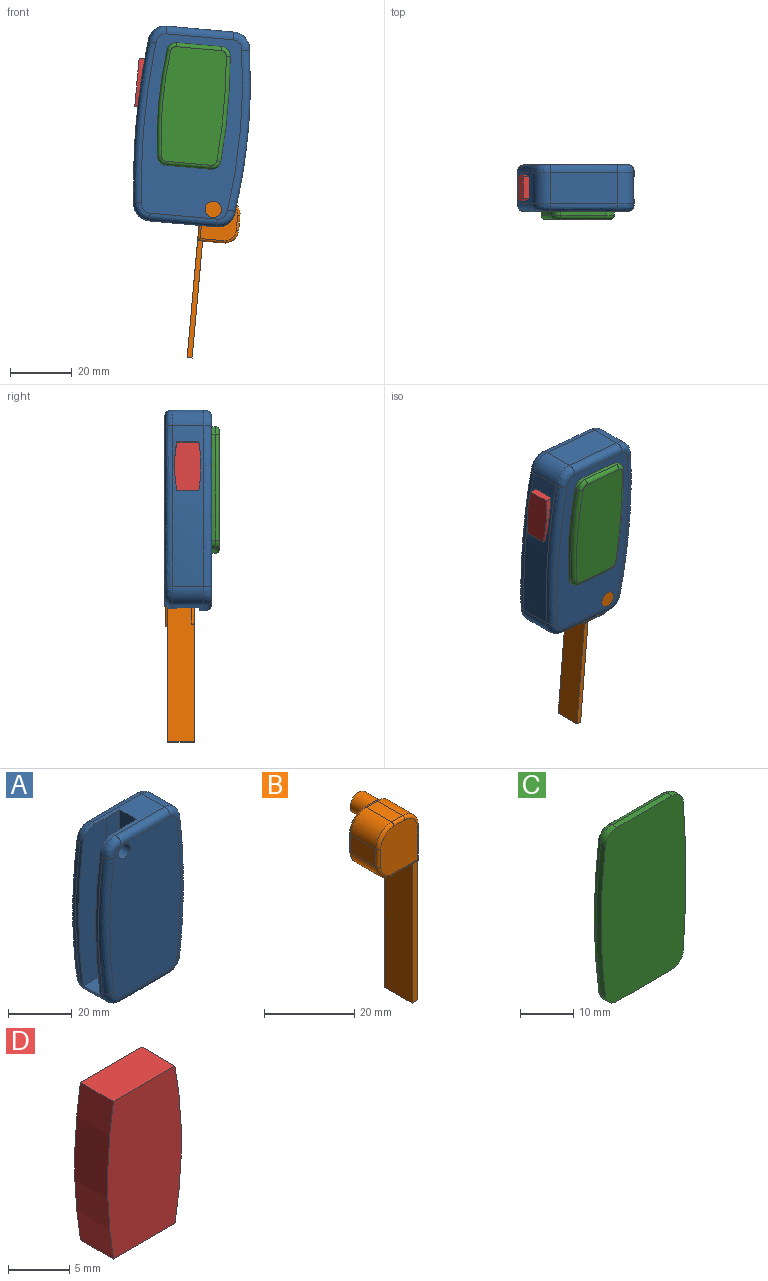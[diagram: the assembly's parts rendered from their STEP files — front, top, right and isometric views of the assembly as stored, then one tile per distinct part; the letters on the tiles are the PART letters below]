
ASSEMBLY  parts=4 mates=3
PART A: 44 faces, bbox 36.5x15.3x63.5 mm
  f0: plane 59.69x7.5mm, normal (-1,0,0), area 368.2mm2, adj f1,f29,f30,f31,f34,f35
  f1: plane 21.84x10.16mm, normal (0,0,1), area 141.2mm2, adj f0,f2,f7,f8,f16,f24,f29,f30
  f2: cylinder r=5.59mm len=5.59mm, axis (0,1,0), area 11.9mm2, adj f1,f3,f26,f29
  f3: cylinder r=183.3mm len=52.32mm, axis (0,1,0), area 71mm2, adj f2,f4,f28,f29
  f4: cylinder r=5.59mm len=10.16mm, axis (0,1,0), area 75.6mm2, adj f3,f9,f10,f19,f27,f29,f30,f31
  f5: cylinder r=5.59mm len=10.16mm, axis (0,1,0), area 89.2mm2, adj f6,f10,f15,f23
  f6: cylinder r=223.52mm len=52.32mm, axis (0,1,0), area 464.3mm2, adj f5,f7,f13,f21,f38,f39,f40,f41
  f7: cylinder r=5.59mm len=10.16mm, axis (0,1,0), area 89.2mm2, adj f1,f6,f14,f22
  f8: cylinder r=5.59mm len=5.59mm, axis (0,1,0), area 11.5mm2, adj f1,f9,f18,f30
  f9: cylinder r=183.3mm len=52.32mm, axis (0,1,0), area 68.7mm2, adj f4,f8,f20,f30
  f10: plane 21.84x10.16mm, normal (0,0,-1), area 221.9mm2, adj f4,f5,f17,f25
  f11: plane 58.43x31.36mm, normal (0,-1,0), area 1720.3mm2, adj f13,f14,f15,f16,f17,f18,f19,f20
  f12: plane 58.43x31.36mm, normal (0,1,0), area 1742.6mm2, adj f21,f22,f23,f24,f25,f26,f27,f28
  f13: bspline ~52.67x4.08mm, area 216.5mm2, adj f6,f11,f14,f15
  f14: bspline ~5.82x5.59mm, area 31mm2, adj f7,f11,f13,f16
  f15: bspline ~6.17x5.62mm, area 31mm2, adj f5,f11,f13,f17
  f16: bspline ~21.84x2.54mm, area 90.2mm2, adj f1,f11,f14,f18
  f17: bspline ~21.84x2.54mm, area 90.2mm2, adj f10,f11,f15,f19
  f18: bspline ~6.22x5.62mm, area 31.1mm2, adj f8,f11,f16,f20
  f19: bspline ~6.22x5.62mm, area 31.1mm2, adj f4,f11,f17,f20
  f20: bspline ~56.81x4.79mm, area 216.7mm2, adj f9,f11,f18,f19
  f21: bspline ~52.67x4.08mm, area 216.5mm2, adj f6,f12,f22,f23
  f22: bspline ~6.17x5.62mm, area 31mm2, adj f7,f12,f21,f24
  f23: bspline ~5.82x5.59mm, area 31mm2, adj f5,f12,f21,f25
  f24: bspline ~21.84x2.54mm, area 90.2mm2, adj f1,f12,f22,f26
  f25: bspline ~21.84x2.54mm, area 90.2mm2, adj f10,f12,f23,f27
  f26: bspline ~6.22x5.62mm, area 31.1mm2, adj f2,f12,f24,f28
  f27: bspline ~6.22x5.62mm, area 31.1mm2, adj f4,f12,f25,f28
  f28: bspline ~56.81x4.79mm, area 216.7mm2, adj f3,f12,f26,f27
  f29: plane 59.69x12.22mm, normal (0,-1,0), area 675.8mm2, adj f0,f1,f2,f3,f4,f31,f32
  f30: plane 59.69x12.22mm, normal (0,1,0), area 653.4mm2, adj f0,f1,f4,f8,f9,f31,f37
  f31: plane 10.05x7.5mm, normal (0,0,1), area 75.3mm2, adj f0,f4,f29,f30
  f32: plane 10.75x0.02mm, normal (1,0,0), area 0.2mm2, adj f1,f29,f33,f35
  f33: plane 10.75x6.1mm, normal (0,-1,0), area 65.6mm2, adj f1,f32,f35,f36
  f34: plane 10.75x6.1mm, normal (0,1,0), area 65.6mm2, adj f0,f1,f35,f36
  f35: plane 7.41x6.1mm, normal (0,0,1), area 45.1mm2, adj f0,f32,f33,f34,f36
  f36: plane 10.75x7.41mm, normal (-1,0,0), area 79.6mm2, adj f1,f33,f34,f35
  f37: cylinder r=2.67mm len=5.33mm, axis (0,1,0), area 64.5mm2, adj f11,f30
  f38: cylinder r=47.15mm len=15.75mm, axis (1,0,0), area 37.3mm2, adj f6,f39,f41,f42,f43
  f39: plane 7.11x1.88mm, normal (0,0,1), area 13.4mm2, adj f6,f38,f40,f43
  f40: cylinder r=42.58mm len=15.75mm, axis (1,0,0), area 37.3mm2, adj f6,f39,f41,f42,f43
  f41: plane 8.49x6.98mm, normal (-1,0,0), area 55.8mm2, adj f6,f38,f40,f42
  f42: plane 7.11x2.54mm, normal (0,0,-1), area 18.1mm2, adj f38,f40,f41,f43
  f43: plane 15.75x8.51mm, normal (1,0,0), area 126.7mm2, adj f38,f39,f40,f42
PART B: 30 faces, bbox 13.8x15x52.7 mm
  f0: plane 7.87x6.83mm, normal (0,0,-1), area 53.8mm2, adj f6,f15,f22,f23
  f1: plane 47.7x8.64mm, normal (1,0,0), area 404.8mm2, adj f2,f14,f21,f24,f25,f26,f27
  f2: cylinder r=4.61mm len=7.87mm, axis (0,1,0), area 57.1mm2, adj f1,f3,f12,f19
  f3: plane 7.87x3.45mm, normal (0,0,1), area 27.1mm2, adj f2,f4,f10,f17
  f4: cylinder r=4.92mm len=7.87mm, axis (0,1,0), area 60.9mm2, adj f3,f5,f9,f16
  f5: plane 7.87x4.79mm, normal (-1,0,0), area 37.7mm2, adj f4,f6,f11,f18
  f6: cylinder r=4.52mm len=7.87mm, axis (0,1,0), area 55.9mm2, adj f0,f5,f13,f20
  f7: plane 12.71x11.46mm, normal (0,-1,0), area 135.7mm2, adj f9,f10,f11,f12,f13,f14,f15
  f8: plane 12.71x11.46mm, normal (0,1,0), area 113.3mm2, adj f16,f17,f18,f19,f20,f21,f22,f28
  f9: torus R=4.16mm, axis (0,-1,0), area 8.7mm2, adj f4,f7,f10,f11
  f10: cylinder r=0.76mm len=3.45mm, axis (1,0,0), area 4.1mm2, adj f3,f7,f9,f12
  f11: cylinder r=0.76mm len=4.79mm, axis (0,0,1), area 5.7mm2, adj f5,f7,f9,f13
  f12: torus R=3.85mm, axis (0,-1,0), area 8.2mm2, adj f2,f7,f10,f14
  f13: torus R=3.76mm, axis (0,-1,0), area 8mm2, adj f6,f7,f11,f15
  f14: cylinder r=0.76mm len=9.62mm, axis (0,0,-1), area 11.2mm2, adj f1,f7,f12,f15
  f15: cylinder r=0.76mm len=8.47mm, axis (-1,0,0), area 9.8mm2, adj f0,f7,f13,f14,f26
  f16: torus R=4.16mm, axis (0,-1,0), area 8.7mm2, adj f4,f8,f17,f18
  f17: cylinder r=0.76mm len=3.45mm, axis (-1,0,0), area 4.1mm2, adj f3,f8,f16,f19
  f18: cylinder r=0.76mm len=4.79mm, axis (0,0,-1), area 5.7mm2, adj f5,f8,f16,f20
  f19: torus R=3.85mm, axis (0,-1,0), area 8.2mm2, adj f2,f8,f17,f21
  f20: torus R=3.76mm, axis (0,-1,0), area 8mm2, adj f6,f8,f18,f22
  f21: cylinder r=0.76mm len=9.43mm, axis (0,0,1), area 11.1mm2, adj f1,f8,f19,f22,f24
  f22: cylinder r=0.76mm len=8.27mm, axis (1,0,0), area 8.9mm2, adj f0,f8,f20,f21,f23,f24
  f23: plane 38.27x8.64mm, normal (-1,0,0), area 329mm2, adj f0,f22,f24,f25,f26,f27
  f24: plane 1.64x0.76mm, normal (0,0,1), area 0.4mm2, adj f1,f21,f22,f23,f27
  f25: plane 8.64x1.64mm, normal (0,0,-1), area 14.1mm2, adj f1,f23,f26,f27
  f26: plane 38.08x1.64mm, normal (0,-1,0), area 62.3mm2, adj f1,f15,f23,f25
  f27: plane 38.27x1.64mm, normal (0,1,0), area 62.6mm2, adj f1,f23,f24,f25
  f28: cylinder r=2.67mm len=5.59mm, axis (0,-1,0), area 93.6mm2, adj f8,f29
  f29: plane 5.33x5.33mm, normal (0,1,0), area 22.3mm2, adj f28
PART C: 18 faces, bbox 24.4x2.5x40.4 mm
  f0: plane 14.58x1.27mm, normal (0,0,1), area 18.5mm2, adj f1,f7,f8,f11
  f1: cylinder r=3.05mm len=3.02mm, axis (0,1,0), area 5.6mm2, adj f0,f2,f8,f13
  f2: cylinder r=130.1mm len=34.62mm, axis (0,1,0), area 44.1mm2, adj f1,f3,f8,f15
  f3: cylinder r=3.05mm len=3.02mm, axis (0,1,0), area 5.6mm2, adj f2,f4,f8,f17
  f4: plane 14.58x1.27mm, normal (0,0,-1), area 18.5mm2, adj f3,f5,f8,f16
  f5: cylinder r=3.05mm len=3.04mm, axis (0,1,0), area 5.8mm2, adj f4,f6,f8,f14
  f6: cylinder r=204.15mm len=34.33mm, axis (0,1,0), area 43.6mm2, adj f5,f7,f8,f12
  f7: cylinder r=3.05mm len=3.04mm, axis (0,1,0), area 5.8mm2, adj f0,f6,f8,f10
  f8: plane 39.91x22.52mm, normal (0,-1,0), area 859.2mm2, adj f0,f1,f2,f3,f4,f5,f6,f7
  f9: plane 37.37x19.98mm, normal (0,1,0), area 716.9mm2, adj f10,f11,f12,f13,f14,f15,f16,f17
  f10: torus R=1.78mm, axis (0,-1,0), area 7.7mm2, adj f7,f9,f11,f12
  f11: cylinder r=1.27mm len=14.58mm, axis (-1,0,0), area 29.1mm2, adj f0,f9,f10,f13
  f12: torus R=202.88mm, axis (0,-1,0), area 68.4mm2, adj f6,f9,f10,f14
  f13: torus R=1.78mm, axis (0,-1,0), area 7.4mm2, adj f1,f9,f11,f15
  f14: torus R=1.78mm, axis (0,-1,0), area 7.7mm2, adj f5,f9,f12,f16
  f15: torus R=128.83mm, axis (0,-1,0), area 69mm2, adj f2,f9,f13,f17
  f16: cylinder r=1.27mm len=14.58mm, axis (1,0,0), area 29.1mm2, adj f4,f9,f14,f17
  f17: torus R=1.78mm, axis (0,-1,0), area 7.4mm2, adj f3,f9,f15,f16
PART D: 6 faces, bbox 8.5x3.8x15.7 mm
  f0: plane 7.11x3.81mm, normal (0,0,1), area 27.1mm2, adj f1,f3,f4,f5
  f1: cylinder r=47.15mm len=15.75mm, axis (0,1,0), area 60.3mm2, adj f0,f2,f4,f5
  f2: plane 7.11x3.81mm, normal (0,0,-1), area 27.1mm2, adj f1,f3,f4,f5
  f3: cylinder r=42.58mm len=15.75mm, axis (0,1,0), area 60.3mm2, adj f0,f2,f4,f5
  f4: plane 15.75x8.51mm, normal (0,-1,0), area 126.7mm2, adj f0,f1,f2,f3
  f5: plane 15.75x8.51mm, normal (0,1,0), area 126.7mm2, adj f0,f1,f2,f3
PLACE A rot(axis=(0,-1,0),174.9deg) t=(0.85,30.27,11.99)mm
PLACE B rot(axis=(-0.04,0,-1),180deg) t=(3.73,20.62,-13.39)mm
PLACE C rot(axis=(-1,0,0.04),180deg) t=(15.74,12.49,44.64)mm
PLACE D rot(axis=(0.04,0.04,1),90.1deg) t=(-16.66,22.5,30.2)mm
MATE fastened C.f8 <-> A.f11  axis (0,1,0) through (1.99,15.03,25.83)mm
MATE revolute B.f28 <-> A.f37  axis (0,-1,0) through (8.42,15.03,-7.72)mm
MATE fastened A.f43 <-> D.f4  axis (-1,0,0.09) through (-13.22,22.75,25.87)mm
